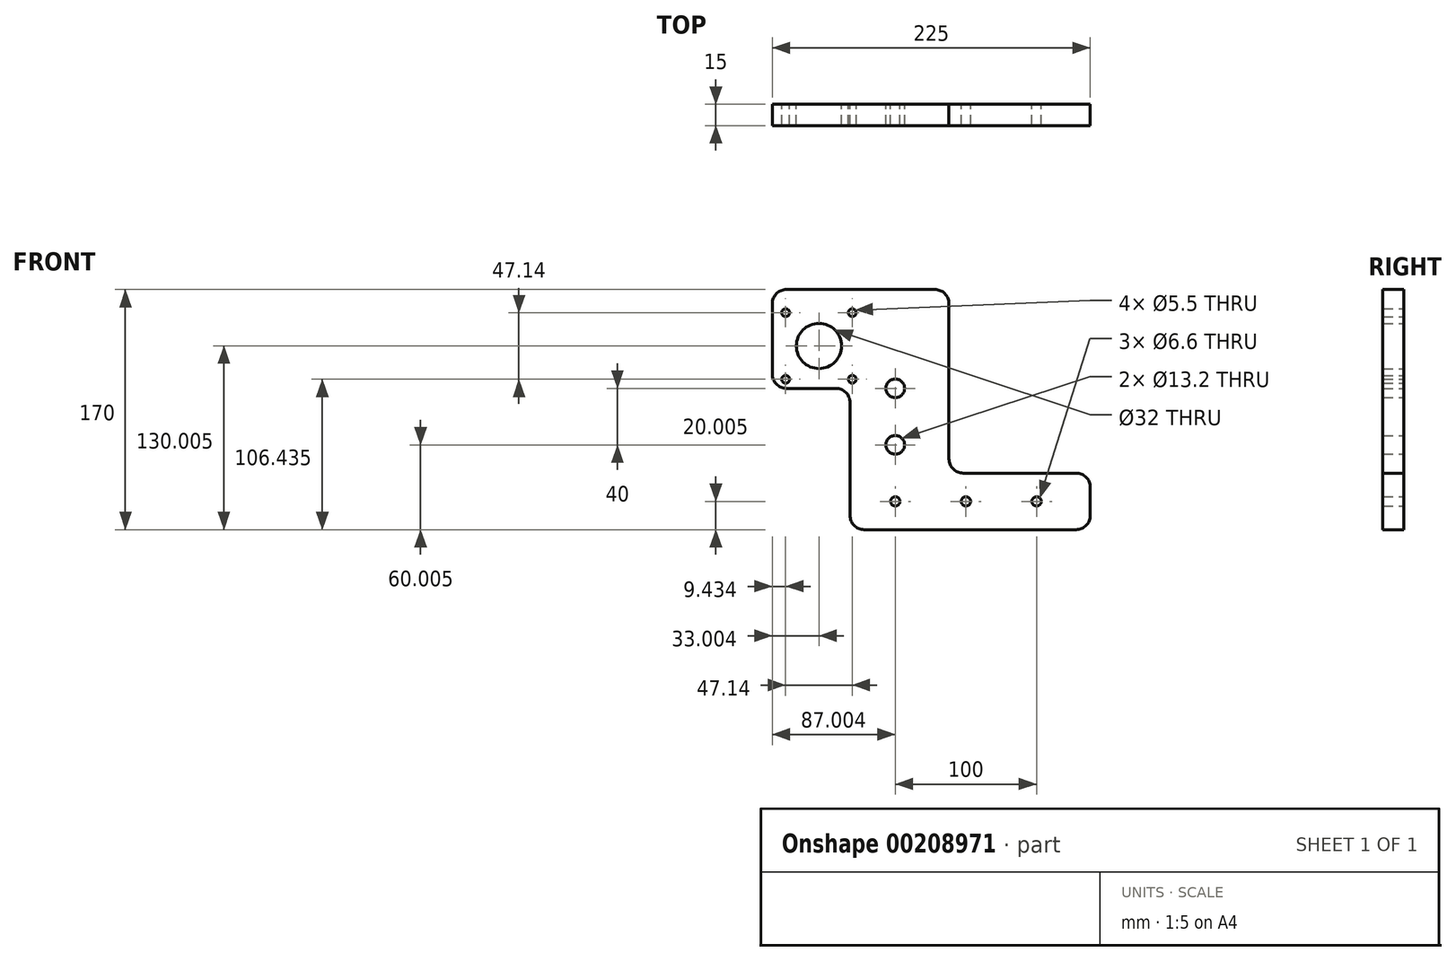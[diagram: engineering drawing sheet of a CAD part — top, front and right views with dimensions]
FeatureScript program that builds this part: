
annotation { "Feature Type Name" : "Feature", "Feature Type Description" : "" }
export const myFeature = defineFeature(function(context is Context, id is Id, definition is map)
    precondition{}
    {
        {
            var Q0;
            Q0=qCreatedBy(makeId("Front.planeOp"),FACE);
            var sketch = newSketch(context, id + "F0", { "sketchPlane" : qUnion([Q0])});
            skLineSegment(sketch, "E0", {"start": v(-57.93, 40.91) * mm, "end": v(62.07, 40.91) * mm});
            skLineSegment(sketch, "E1", {"start": v(62.07, 40.91) * mm, "end": v(62.07, -89.09) * mm});
            skLineSegment(sketch, "E2", {"start": v(62.07, -89.09) * mm, "end": v(162.07, -89.09) * mm});
            skLineSegment(sketch, "E3", {"start": v(162.07, -89.09) * mm, "end": v(162.07, -129.09) * mm});
            skLineSegment(sketch, "E4", {"start": v(162.07, -129.09) * mm, "end": v(-7.93, -129.09) * mm});
            skLineSegment(sketch, "E5", {"start": v(-7.93, -129.09) * mm, "end": v(-7.93, -29.09) * mm});
            skLineSegment(sketch, "E6", {"start": v(-7.93, -29.09) * mm, "end": v(-57.93, -29.09) * mm});
            skLineSegment(sketch, "E7", {"start": v(52.07, 30.91) * mm, "end": v(-47.93, 30.91) * mm, "construction": true});
            skLineSegment(sketch, "E8", {"start": v(-47.93, 30.91) * mm, "end": v(-47.93, -19.09) * mm, "construction": true});
            skLineSegment(sketch, "E9", {"start": v(-47.93, -19.09) * mm, "end": v(4.07, -19.09) * mm, "construction": true});
            skLineSegment(sketch, "E10", {"start": v(4.07, -19.09) * mm, "end": v(4.07, -129.09) * mm, "construction": true});
            skLineSegment(sketch, "E11", {"start": v(4.07, -129.09) * mm, "end": v(162.07, -129.09) * mm, "construction": true});
            skLineSegment(sketch, "E12", {"start": v(162.07, -129.09) * mm, "end": v(162.07, -89.09) * mm, "construction": true});
            skLineSegment(sketch, "E13", {"start": v(162.07, -89.09) * mm, "end": v(52.07, -89.09) * mm, "construction": true});
            skLineSegment(sketch, "E14", {"start": v(52.07, -89.09) * mm, "end": v(52.07, 30.91) * mm, "construction": true});
            skPoint(sketch, "E15", {"position": v(24.07, -109.09) * mm});
            skPoint(sketch, "E16", {"position": v(24.07, -69.09) * mm});
            skPoint(sketch, "E17", {"position": v(24.07, -29.09) * mm});
            skPoint(sketch, "E18", {"position": v(74.07, -109.09) * mm});
            skPoint(sketch, "E19", {"position": v(124.07, -109.09) * mm});
            skPoint(sketch, "E20", {"position": v(-29.93, 0.91) * mm});
            skPoint(sketch, "E21", {"position": v(-53.5, 24.48) * mm});
            skLineSegment(sketch, "E22", {"start": v(-44.33, 0.91) * mm, "end": v(-15.97, 0.91) * mm, "construction": true});
            skLineSegment(sketch, "E23", {"start": v(-29.93, 17.3) * mm, "end": v(-29.93, -11.44) * mm, "construction": true});
            skPoint(sketch, "E24.MirrorP", {"position": v(-53.5, -22.66) * mm});
            skPoint(sketch, "E25.MirrorP", {"position": v(-6.36, 24.48) * mm});
            skPoint(sketch, "E26.MirrorP", {"position": v(-6.36, -22.66) * mm});
            skLineSegment(sketch, "E27", {"start": v(-57.93, 40.91) * mm, "end": v(-62.93, 40.91) * mm});
            skLineSegment(sketch, "E28", {"start": v(-62.93, 40.91) * mm, "end": v(-62.93, -29.09) * mm});
            skLineSegment(sketch, "E29", {"start": v(-62.93, -29.09) * mm, "end": v(-57.93, -29.09) * mm});
            skSolve(sketch);
        }
        {
            var Q0;
            Q0=makeQuery(id+"F0.imprint","IMPRINT",FACE,{"disambiguationData":[TD([[makeQuery(id+"F0.imprint","IMPRINT",EDGE,{"derivedFrom":sQuery(id+"F0.wireOp",EDGE,"E0")}),-1.0]])]});
            extrude(context, id + "F1", {"entities" : qUnion([Q0]), "depth" : 15 * mm});
        }
        {
            var Q0;
            Q0=sQuery(id+"F0.wireOp",VERTEX,"E16");
            var Q1;
            Q1=sQuery(id+"F0.wireOp",VERTEX,"E17");
            var Q2;
            Q2=makeQuery(id+"F1.opExtrude","SWEPT_BODY",BODY,{"disambiguationData":[OSD([sQuery(id+"F0.wireOp",EDGE,"E0"),sQuery(id+"F0.wireOp",EDGE,"E1"),sQuery(id+"F0.wireOp",EDGE,"E2"),sQuery(id+"F0.wireOp",EDGE,"E3"),sQuery(id+"F0.wireOp",EDGE,"E4"),sQuery(id+"F0.wireOp",EDGE,"E5"),sQuery(id+"F0.wireOp",EDGE,"E6"),sQuery(id+"F0.wireOp",EDGE,"cvZF5QLb-uWAo-robz-iAHo-1Gj3ORty2Von")])]});
            hole(context, id + "F2", {"style" : HoleStyle.SIMPLE, "endStyle" : HoleEndStyle.THROUGH, "oppositeDirection" : true, "standardTappedOrClearance" : lookupTablePath({ "standard" : "ISO", "fit" : "Normal", "size" : "M12", "type" : "Clearance" }), "standardBlindInLast" : lookupTablePath({ "fit" : "Standard", "standard" : "ISO", "size" : "M12", "type" : "Clearance" }), "holeDiameter" : 13.2 * mm, "locations" : qUnion([Q0, Q1]), "scope" : qUnion([Q2]), "isTappedThrough" : true});
        }
        {
            var Q0;
            Q0=sQuery(id+"F0.wireOp",VERTEX,"E15");
            var Q1;
            Q1=sQuery(id+"F0.wireOp",VERTEX,"E18");
            var Q2;
            Q2=sQuery(id+"F0.wireOp",VERTEX,"E19");
            var Q3;
            Q3=makeQuery(id+"F1.opExtrude","SWEPT_BODY",BODY,{"disambiguationData":[OSD([sQuery(id+"F0.wireOp",EDGE,"E0"),sQuery(id+"F0.wireOp",EDGE,"E1"),sQuery(id+"F0.wireOp",EDGE,"E2"),sQuery(id+"F0.wireOp",EDGE,"E3"),sQuery(id+"F0.wireOp",EDGE,"E4"),sQuery(id+"F0.wireOp",EDGE,"E5"),sQuery(id+"F0.wireOp",EDGE,"E6"),sQuery(id+"F0.wireOp",EDGE,"cvZF5QLb-uWAo-robz-iAHo-1Gj3ORty2Von")])]});
            hole(context, id + "F3", {"style" : HoleStyle.SIMPLE, "endStyle" : HoleEndStyle.THROUGH, "oppositeDirection" : true, "standardTappedOrClearance" : lookupTablePath({ "standard" : "ISO", "fit" : "Normal", "size" : "M6", "type" : "Clearance" }), "standardBlindInLast" : lookupTablePath({ "fit" : "Standard", "standard" : "ISO", "size" : "M6", "type" : "Clearance" }), "holeDiameter" : 6.6 * mm, "locations" : qUnion([Q0, Q1, Q2]), "scope" : qUnion([Q3]), "isTappedThrough" : true});
        }
        {
            var Q0;
            Q0=makeQuery(id+"F1.opExtrude","SWEPT_EDGE",EDGE,{"disambiguationData":[OSD([sQuery(id+"F0.wireOp",EDGE,"E0"),sQuery(id+"F0.wireOp",EDGE,"cvZF5QLb-uWAo-robz-iAHo-1Gj3ORty2Von")])]});
            var Q1;
            Q1=makeQuery(id+"F1.opExtrude","SWEPT_EDGE",EDGE,{"disambiguationData":[OSD([sQuery(id+"F0.wireOp",EDGE,"E1"),sQuery(id+"F0.wireOp",EDGE,"E2")])]});
            var Q2;
            Q2=makeQuery(id+"F1.opExtrude","SWEPT_EDGE",EDGE,{"disambiguationData":[OSD([sQuery(id+"F0.wireOp",EDGE,"E0"),sQuery(id+"F0.wireOp",EDGE,"E1")])]});
            var Q3;
            Q3=makeQuery(id+"F1.opExtrude","SWEPT_EDGE",EDGE,{"disambiguationData":[OSD([sQuery(id+"F0.wireOp",EDGE,"E3"),sQuery(id+"F0.wireOp",EDGE,"E4")])]});
            var Q4;
            Q4=makeQuery(id+"F1.opExtrude","SWEPT_EDGE",EDGE,{"disambiguationData":[OSD([sQuery(id+"F0.wireOp",EDGE,"E2"),sQuery(id+"F0.wireOp",EDGE,"E3")])]});
            var Q5;
            Q5=makeQuery(id+"F1.opExtrude","SWEPT_EDGE",EDGE,{"disambiguationData":[OSD([sQuery(id+"F0.wireOp",EDGE,"E4"),sQuery(id+"F0.wireOp",EDGE,"E5")])]});
            var Q6;
            Q6=makeQuery(id+"F1.opExtrude","SWEPT_EDGE",EDGE,{"disambiguationData":[OSD([sQuery(id+"F0.wireOp",EDGE,"E5"),sQuery(id+"F0.wireOp",EDGE,"E6")])]});
            var Q7;
            Q7=makeQuery(id+"F1.opExtrude","SWEPT_EDGE",EDGE,{"disambiguationData":[OSD([sQuery(id+"F0.wireOp",EDGE,"E6"),sQuery(id+"F0.wireOp",EDGE,"cvZF5QLb-uWAo-robz-iAHo-1Gj3ORty2Von")])]});
            var Q8;
            Q8=makeQuery(id+"F1.opExtrude","SWEPT_EDGE",EDGE,{"disambiguationData":[OSD([sQuery(id+"F0.wireOp",EDGE,"E27"),sQuery(id+"F0.wireOp",EDGE,"E28")])]});
            var Q9;
            Q9=makeQuery(id+"F1.opExtrude","SWEPT_EDGE",EDGE,{"disambiguationData":[OSD([sQuery(id+"F0.wireOp",EDGE,"E28"),sQuery(id+"F0.wireOp",EDGE,"E29")])]});
            fillet(context, id + "F4", {"entities" : qUnion([Q0, Q1, Q2, Q3, Q4, Q5, Q6, Q7, Q8, Q9]), "radius" : 10 * mm, "tangentPropagation" : true, "allowEdgeOverflow" : false});
        }
        {
            var Q0;
            Q0=sQuery(id+"F0.wireOp",VERTEX,"E20");
            var Q1;
            Q1=makeQuery(id+"F1.opExtrude","SWEPT_BODY",BODY,{"disambiguationData":[OSD([sQuery(id+"F0.wireOp",EDGE,"E0"),sQuery(id+"F0.wireOp",EDGE,"E1"),sQuery(id+"F0.wireOp",EDGE,"E2"),sQuery(id+"F0.wireOp",EDGE,"E3"),sQuery(id+"F0.wireOp",EDGE,"E4"),sQuery(id+"F0.wireOp",EDGE,"E5"),sQuery(id+"F0.wireOp",EDGE,"E6"),sQuery(id+"F0.wireOp",EDGE,"cvZF5QLb-uWAo-robz-iAHo-1Gj3ORty2Von")])]});
            hole(context, id + "F5", {"style" : HoleStyle.SIMPLE, "endStyle" : HoleEndStyle.THROUGH, "oppositeDirection" : true, "holeDiameter" : 32 * mm, "locations" : qUnion([Q0]), "scope" : qUnion([Q1]), "isTappedThrough" : true});
        }
        {
            var Q0;
            Q0=sQuery(id+"F0.wireOp",VERTEX,"E21");
            var Q1;
            Q1=sQuery(id+"F0.wireOp",VERTEX,"E25.MirrorP");
            var Q2;
            Q2=sQuery(id+"F0.wireOp",VERTEX,"E26.MirrorP");
            var Q3;
            Q3=sQuery(id+"F0.wireOp",VERTEX,"E24.MirrorP");
            var Q4;
            Q4=makeQuery(id+"F1.opExtrude","SWEPT_BODY",BODY,{"disambiguationData":[OSD([sQuery(id+"F0.wireOp",EDGE,"E0"),sQuery(id+"F0.wireOp",EDGE,"E1"),sQuery(id+"F0.wireOp",EDGE,"E2"),sQuery(id+"F0.wireOp",EDGE,"E3"),sQuery(id+"F0.wireOp",EDGE,"E4"),sQuery(id+"F0.wireOp",EDGE,"E5"),sQuery(id+"F0.wireOp",EDGE,"E6"),sQuery(id+"F0.wireOp",EDGE,"cvZF5QLb-uWAo-robz-iAHo-1Gj3ORty2Von")])]});
            hole(context, id + "F6", {"style" : HoleStyle.SIMPLE, "endStyle" : HoleEndStyle.THROUGH, "oppositeDirection" : true, "standardTappedOrClearance" : lookupTablePath({ "standard" : "ISO", "fit" : "Normal", "size" : "M5", "type" : "Clearance" }), "standardBlindInLast" : lookupTablePath({ "fit" : "Standard", "standard" : "ISO", "size" : "M5", "type" : "Clearance" }), "holeDiameter" : 5.5 * mm, "locations" : qUnion([Q0, Q1, Q2, Q3]), "scope" : qUnion([Q4]), "isTappedThrough" : true});
        }
    });
